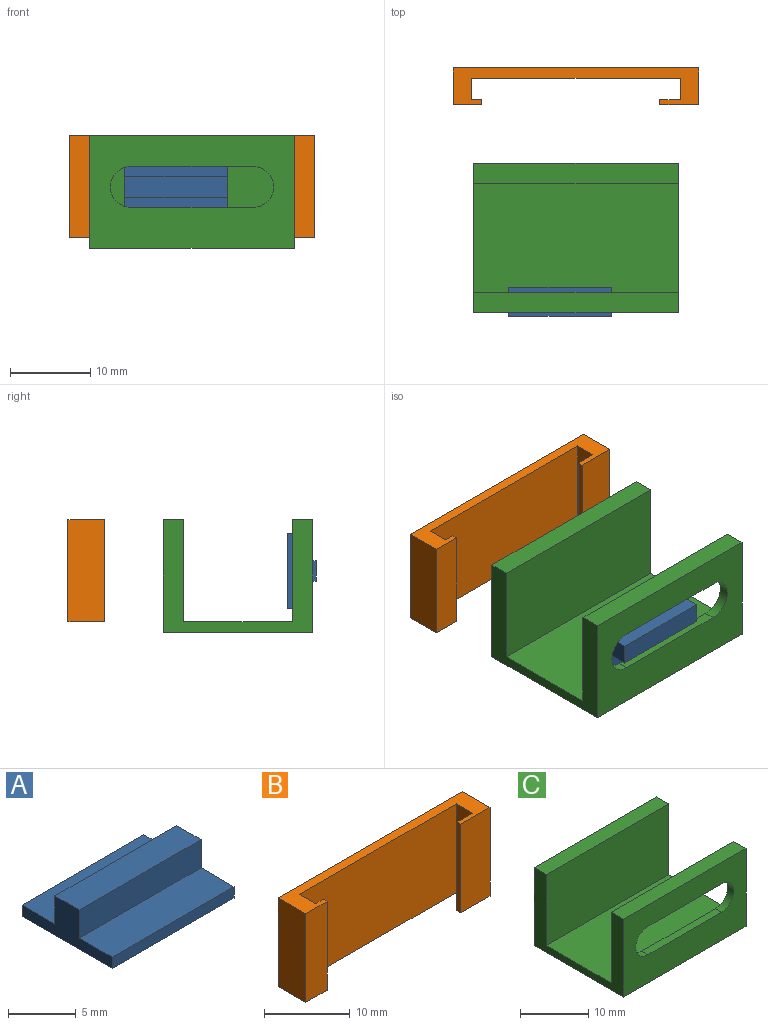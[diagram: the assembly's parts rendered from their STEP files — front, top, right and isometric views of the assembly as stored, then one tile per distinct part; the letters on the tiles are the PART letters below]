
ASSEMBLY  parts=3 mates=2
PART A: 10 faces, bbox 12.7x9.4x3.6 mm
  f0: plane 12.7x3.43mm, normal (0,0,1), area 43.5mm2, adj f1,f2,f4,f7
  f1: plane 12.7x1.02mm, normal (0,-1,0), area 12.9mm2, adj f0,f2,f4,f6
  f2: plane 9.4x3.56mm, normal (1,0,0), area 16mm2, adj f0,f1,f3,f5,f6,f7,f8,f9
  f3: plane 12.7x1.02mm, normal (0,1,0), area 12.9mm2, adj f2,f4,f5,f6
  f4: plane 9.4x3.56mm, normal (-1,0,0), area 16mm2, adj f0,f1,f3,f5,f6,f7,f8,f9
  f5: plane 12.7x3.43mm, normal (0,0,1), area 43.5mm2, adj f2,f3,f4,f8
  f6: plane 12.7x9.4mm, normal (0,0,-1), area 119.4mm2, adj f1,f2,f3,f4
  f7: plane 12.7x2.54mm, normal (0,-1,0), area 32.3mm2, adj f0,f2,f4,f9
  f8: plane 12.7x2.54mm, normal (0,1,0), area 32.3mm2, adj f2,f4,f5,f9
  f9: plane 12.7x2.54mm, normal (0,0,1), area 32.3mm2, adj f2,f4,f7,f8
PART B: 14 faces, bbox 30.5x4.6x12.7 mm
  f0: plane 12.7x2.67mm, normal (-1,0,0), area 33.9mm2, adj f2,f6,f7,f12
  f1: plane 12.7x2.67mm, normal (1,0,0), area 33.9mm2, adj f2,f6,f7,f10
  f2: plane 25.91x12.7mm, normal (0,-1,0), area 329mm2, adj f0,f1,f6,f7
  f3: plane 12.7x4.57mm, normal (1,0,0), area 58.1mm2, adj f4,f6,f7,f9
  f4: plane 30.48x12.7mm, normal (0,1,0), area 387.1mm2, adj f3,f5,f6,f7
  f5: plane 12.7x4.57mm, normal (-1,0,0), area 58.1mm2, adj f4,f6,f7,f8
  f6: plane 30.48x4.57mm, normal (0,0,1), area 56.2mm2, adj f0,f1,f2,f3,f4,f5,f8,f9
  f7: plane 30.48x4.57mm, normal (0,0,-1), area 56.2mm2, adj f0,f1,f2,f3,f4,f5,f8,f9
  f8: plane 12.7x3.56mm, normal (0,-1,0), area 45.2mm2, adj f5,f6,f7,f11
  f9: plane 12.7x4.83mm, normal (0,-1,0), area 61.3mm2, adj f3,f6,f7,f13
  f10: plane 12.7x1.27mm, normal (0,1,0), area 16.1mm2, adj f1,f6,f7,f11
  f11: plane 12.7x0.64mm, normal (1,0,0), area 8.1mm2, adj f6,f7,f8,f10
  f12: plane 12.7x2.54mm, normal (0,1,0), area 32.3mm2, adj f0,f6,f7,f13
  f13: plane 12.7x0.64mm, normal (-1,0,0), area 8.1mm2, adj f6,f7,f9,f12
PART C: 19 faces, bbox 25.4x18.5x14 mm
  f0: plane 25.4x12.7mm, normal (0,1,0), area 90.3mm2, adj f5,f7,f9,f13,f15,f16,f17,f18
  f1: cylinder r=2.54mm len=5.08mm, axis (0,-1,0), area 10.1mm2, adj f2,f4,f6,f14
  f2: plane 15.24x1.27mm, normal (0,0,1), area 19.4mm2, adj f1,f3,f6,f14
  f3: cylinder r=2.54mm len=5.08mm, axis (0,-1,0), area 10.1mm2, adj f2,f4,f6,f14
  f4: plane 15.24x1.27mm, normal (0,0,-1), area 19.4mm2, adj f1,f3,f6,f14
  f5: plane 25.4x13.46mm, normal (0,0,1), area 341.9mm2, adj f0,f7,f9,f11
  f6: plane 25.4x13.97mm, normal (0,-1,0), area 257.2mm2, adj f1,f2,f3,f4,f7,f9,f10,f13
  f7: plane 18.54x13.97mm, normal (1,0,0), area 88.1mm2, adj f0,f5,f6,f8,f10,f11,f12,f13
  f8: plane 25.4x13.97mm, normal (0,1,0), area 354.8mm2, adj f7,f9,f10,f12
  f9: plane 18.54x13.97mm, normal (-1,0,0), area 88.1mm2, adj f0,f5,f6,f8,f10,f11,f12,f13
  f10: plane 25.4x18.54mm, normal (0,0,-1), area 471mm2, adj f6,f7,f8,f9
  f11: plane 25.4x12.7mm, normal (0,-1,0), area 322.6mm2, adj f5,f7,f9,f12
  f12: plane 25.4x2.54mm, normal (0,0,1), area 64.5mm2, adj f7,f8,f9,f11
  f13: plane 25.4x2.54mm, normal (0,0,1), area 64.5mm2, adj f0,f6,f7,f9
  f14: plane 22.86x10.16mm, normal (0,1,0), area 134.6mm2, adj f1,f2,f3,f4,f15,f16,f17,f18
  f15: plane 22.86x1.27mm, normal (0,0,1), area 29mm2, adj f0,f14,f16,f18
  f16: plane 10.16x1.27mm, normal (1,0,0), area 12.9mm2, adj f0,f14,f15,f17
  f17: plane 22.86x1.27mm, normal (0,0,-1), area 29mm2, adj f0,f14,f16,f18
  f18: plane 10.16x1.27mm, normal (-1,0,0), area 12.9mm2, adj f0,f14,f15,f17
PLACE A rot(axis=(1,0,0),90deg) t=(1.24,0.32,7.53)mm
PLACE B t=(3.22,26.95,1.18)mm
PLACE C t=(3.22,6.46,-0.09)mm fixed
MATE slider B.f2 <-> C.f0  axis (0,-1,0) through (3.22,26.31,13.88)mm
MATE slider A.f4 <-> C.f16  axis (-1,0,0) through (-5.11,-0.91,7.53)mm
